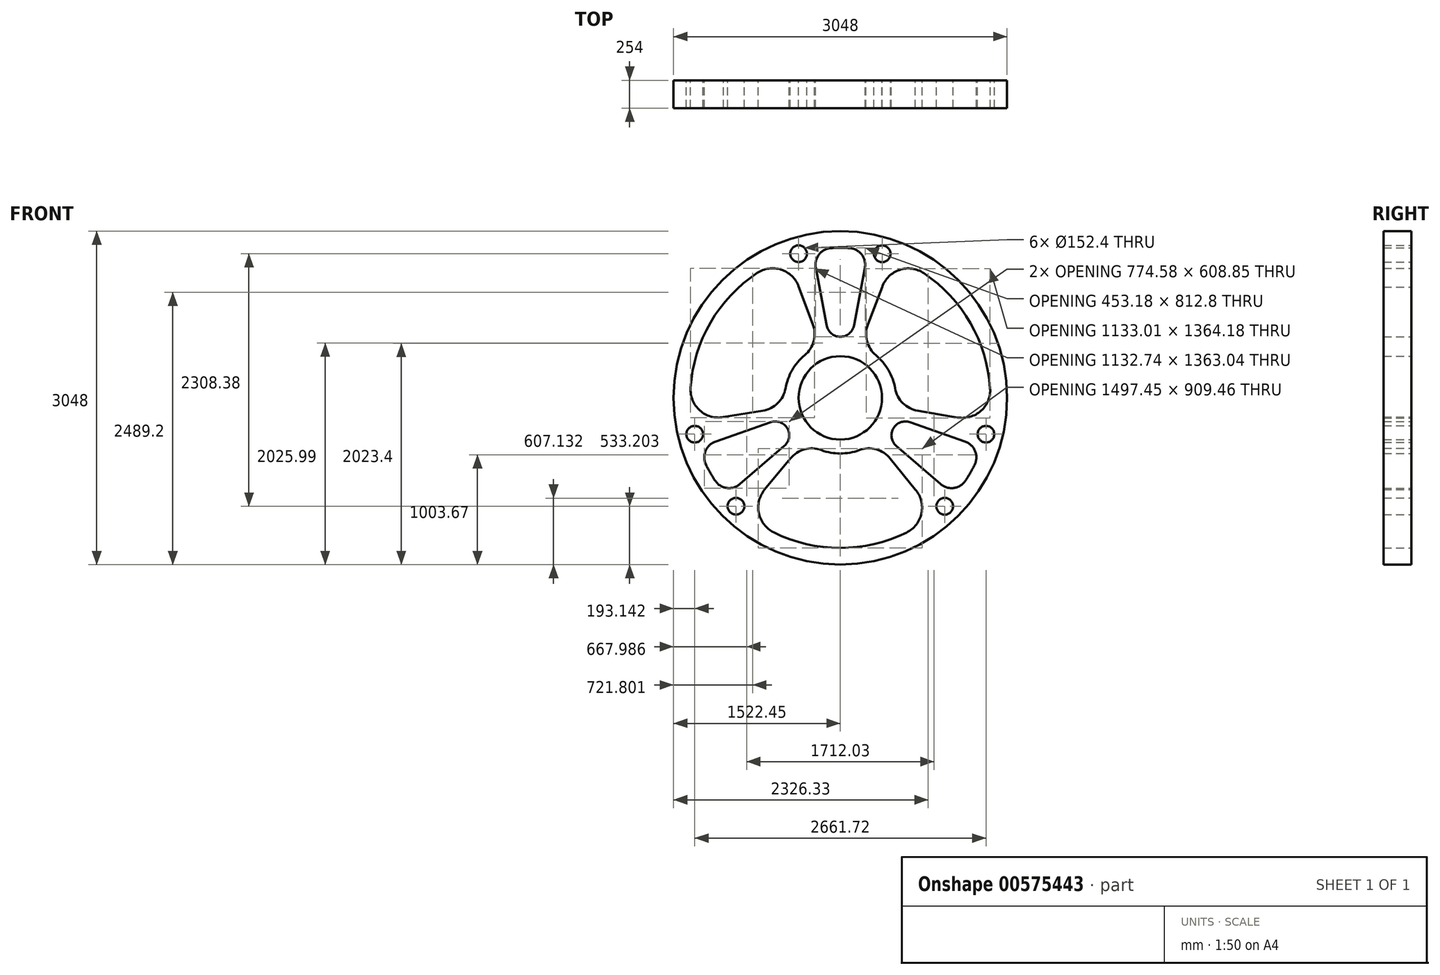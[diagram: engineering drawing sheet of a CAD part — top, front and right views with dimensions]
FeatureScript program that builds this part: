
annotation { "Feature Type Name" : "Feature", "Feature Type Description" : "" }
export const myFeature = defineFeature(function(context is Context, id is Id, definition is map)
    precondition{}
    {
        {
            var Q0;
            Q0=qCreatedBy(makeId("Front.planeOp"),FACE);
            var sketch = newSketch(context, id + "F0", { "sketchPlane" : qUnion([Q0])});
            skCircle(sketch, "E0", {"center": v(0, 0) * mm, "radius": 1524 * mm});
            skArc(sketch, "E1", {"start": v(-173.99, -477.28) * mm, "mid": v(0, -508) * mm, "end": v(173.99, -477.28) * mm});
            skLineSegment(sketch, "E2", {"start": v(0, 0) * mm, "end": v(0, 0) * mm});
            skArc(sketch, "E3", {"start": v(-173.99, -477.28) * mm, "mid": v(-327.72, -470.84) * mm, "end": v(-456.96, -554.34) * mm});
            skArc(sketch, "E4", {"start": v(-692.3, -839.79) * mm, "mid": v(-744.7, -1054.46) * mm, "end": v(-609.1, -1228.94) * mm});
            skArc(sketch, "E5", {"start": v(456.97, -554.35) * mm, "mid": v(327.73, -470.84) * mm, "end": v(173.99, -477.28) * mm});
            skArc(sketch, "E6", {"start": v(605.37, -1230.78) * mm, "mid": v(742.1, -1053.78) * mm, "end": v(685.9, -837.3) * mm});
            skArc(sketch, "E7.trimOffspring", {"start": v(500.33, 87.96) * mm, "mid": v(439.94, 254) * mm, "end": v(326.34, 389.31) * mm});
            skLineSegment(sketch, "E8.trimOffspring", {"start": v(-456.96, -554.34) * mm, "end": v(-692.3, -839.79) * mm});
            skLineSegment(sketch, "E9.trimOffspring", {"start": v(456.97, -554.35) * mm, "end": v(685.9, -837.3) * mm});
            skArc(sketch, "E10", {"start": v(-83.52, 1369.05) * mm, "mid": v(-194.47, 1310.6) * mm, "end": v(-224, 1188.72) * mm});
            skArc(sketch, "E11", {"start": v(224, 1188.72) * mm, "mid": v(194.47, 1310.6) * mm, "end": v(83.52, 1369.05) * mm});
            skArc(sketch, "E12", {"start": v(-124.8, 662.28) * mm, "mid": v(0, 558.8) * mm, "end": v(124.8, 662.28) * mm});
            skLineSegment(sketch, "E13", {"start": v(-224, 1188.72) * mm, "end": v(-124.8, 662.28) * mm});
            skLineSegment(sketch, "E14", {"start": v(224, 1188.72) * mm, "end": v(124.8, 662.28) * mm});
            skArc(sketch, "E15.trimOffspring", {"start": v(83.52, 1369.05) * mm, "mid": v(0, 1371.6) * mm, "end": v(-83.52, 1369.05) * mm});
            skLineSegment(sketch, "E16.trimOffspring", {"start": v(124.8, 662.28) * mm, "end": v(224, 1188.72) * mm});
            skLineSegment(sketch, "E17.trimOffspring", {"start": v(-124.8, 662.28) * mm, "end": v(-224, 1188.72) * mm});
            skArc(sketch, "E18.1.0", {"start": v(251.6, 672.92) * mm, "mid": v(243.9, 519.24) * mm, "end": v(326.34, 389.31) * mm});
            skArc(sketch, "E18.1.2", {"start": v(500.33, 87.96) * mm, "mid": v(571.62, -48.4) * mm, "end": v(708.55, -118.57) * mm});
            skLineSegment(sketch, "E18.1.3", {"start": v(708.55, -118.57) * mm, "end": v(1073.42, -179.65) * mm});
            skArc(sketch, "E18.1.4", {"start": v(1073.42, -179.65) * mm, "mid": v(1285.53, -117.7) * mm, "end": v(1368.84, 86.97) * mm});
            skArc(sketch, "E18.1.5", {"start": v(763.2, 1139.65) * mm, "mid": v(541.55, 1169.57) * mm, "end": v(382.17, 1012.65) * mm});
            skLineSegment(sketch, "E18.1.6", {"start": v(251.6, 672.92) * mm, "end": v(382.17, 1012.65) * mm});
            skArc(sketch, "E18.2.0", {"start": v(-708.57, -118.57) * mm, "mid": v(-571.62, -48.4) * mm, "end": v(-500.33, 87.96) * mm});
            skArc(sketch, "E18.2.2", {"start": v(-326.34, 389.31) * mm, "mid": v(-243.9, 519.23) * mm, "end": v(-251.6, 672.91) * mm});
            skLineSegment(sketch, "E18.2.3", {"start": v(-251.6, 672.91) * mm, "end": v(-381.13, 1019.44) * mm});
            skArc(sketch, "E18.2.4", {"start": v(-381.13, 1019.44) * mm, "mid": v(-540.84, 1172.15) * mm, "end": v(-759.74, 1141.96) * mm});
            skArc(sketch, "E18.2.5", {"start": v(-1368.57, 91.12) * mm, "mid": v(-1283.65, -115.8) * mm, "end": v(-1068.07, -175.35) * mm});
            skLineSegment(sketch, "E18.2.6", {"start": v(-708.57, -118.57) * mm, "end": v(-1068.07, -175.35) * mm});
            skLineSegment(sketch, "E19.1.0", {"start": v(-635.95, -223.06) * mm, "end": v(-1141.46, -400.36) * mm});
            skLineSegment(sketch, "E19.1.1", {"start": v(-917.45, -788.35) * mm, "end": v(-511.15, -439.22) * mm});
            skArc(sketch, "E19.1.2", {"start": v(-1143.87, -756.86) * mm, "mid": v(-1037.77, -823.71) * mm, "end": v(-917.45, -788.35) * mm});
            skArc(sketch, "E19.1.3", {"start": v(-1227.4, -612.2) * mm, "mid": v(-1187.84, -685.8) * mm, "end": v(-1143.87, -756.86) * mm});
            skArc(sketch, "E19.1.4", {"start": v(-1141.46, -400.36) * mm, "mid": v(-1232.24, -486.88) * mm, "end": v(-1227.4, -612.2) * mm});
            skArc(sketch, "E19.1.5", {"start": v(-511.15, -439.22) * mm, "mid": v(-483.93, -279.4) * mm, "end": v(-635.95, -223.06) * mm});
            skLineSegment(sketch, "E19.2.0", {"start": v(511.15, -439.22) * mm, "end": v(917.45, -788.35) * mm});
            skLineSegment(sketch, "E19.2.1", {"start": v(1141.46, -400.36) * mm, "end": v(635.95, -223.06) * mm});
            skArc(sketch, "E19.2.2", {"start": v(1227.4, -612.2) * mm, "mid": v(1232.24, -486.88) * mm, "end": v(1141.46, -400.36) * mm});
            skArc(sketch, "E19.2.3", {"start": v(1143.87, -756.86) * mm, "mid": v(1187.84, -685.8) * mm, "end": v(1227.4, -612.2) * mm});
            skArc(sketch, "E19.2.4", {"start": v(917.45, -788.35) * mm, "mid": v(1037.77, -823.71) * mm, "end": v(1143.87, -756.86) * mm});
            skArc(sketch, "E19.2.5", {"start": v(635.95, -223.06) * mm, "mid": v(483.93, -279.4) * mm, "end": v(511.15, -439.22) * mm});
            skCircle(sketch, "E20", {"center": v(-381.13, 1317.58) * mm, "radius": 76.2 * mm});
            skCircle(sketch, "E21.1.0", {"center": v(-953.56, -989.74) * mm, "radius": 76.2 * mm});
            skCircle(sketch, "E21.2.0", {"center": v(1330.86, -331.82) * mm, "radius": 76.2 * mm});
            skPoint(sketch, "E21.center", {"position": v(-1.28, -1.33) * mm});
            skCircle(sketch, "E22", {"center": v(382.17, 1317.28) * mm, "radius": 76.2 * mm});
            skCircle(sketch, "E23.1.0", {"center": v(-1330.86, -331.82) * mm, "radius": 76.2 * mm});
            skCircle(sketch, "E23.2.0", {"center": v(953.82, -990.8) * mm, "radius": 76.2 * mm});
            skPoint(sketch, "E23.center", {"position": v(1.71, -1.78) * mm});
            skArc(sketch, "E24.trimOffspring", {"start": v(-326.34, 389.31) * mm, "mid": v(-439.94, 254) * mm, "end": v(-500.33, 87.96) * mm});
            skPoint(sketch, "E25.orphan", {"position": v(326.34, 389.31) * mm});
            skPoint(sketch, "E26.orphan", {"position": v(-326.34, 389.31) * mm});
            skCircle(sketch, "E27", {"center": v(0, 0) * mm, "radius": 381 * mm});
            skArc(sketch, "E28", {"start": v(-98.43, -25.2) * mm, "mid": v(-71.84, -71.84) * mm, "end": v(-25.2, -98.42) * mm});
            skArc(sketch, "E29", {"start": v(-25.2, -98.43) * mm, "mid": v(0, -127) * mm, "end": v(25.2, -98.43) * mm});
            skArc(sketch, "E30", {"start": v(98.43, -25.2) * mm, "mid": v(127, 0) * mm, "end": v(98.43, 25.2) * mm});
            skArc(sketch, "E31", {"start": v(-98.43, 25.2) * mm, "mid": v(-127, 0) * mm, "end": v(-98.43, -25.2) * mm});
            skArc(sketch, "E32", {"start": v(25.2, 98.43) * mm, "mid": v(0, 127) * mm, "end": v(-25.2, 98.43) * mm});
            skArc(sketch, "E33.trimOffspring", {"start": v(98.43, 25.2) * mm, "mid": v(71.84, 71.84) * mm, "end": v(25.2, 98.43) * mm});
            skArc(sketch, "E34.trimOffspring", {"start": v(25.2, -98.43) * mm, "mid": v(71.84, -71.84) * mm, "end": v(98.42, -25.2) * mm});
            skArc(sketch, "E35.trimOffspring", {"start": v(-25.2, 98.43) * mm, "mid": v(-71.84, 71.84) * mm, "end": v(-98.42, 25.2) * mm});
            skCircle(sketch, "E36", {"center": v(101.6, 113.6) * mm, "radius": 50.8 * mm});
            skCircle(sketch, "E37", {"center": v(101.6, -113.6) * mm, "radius": 50.8 * mm});
            skCircle(sketch, "E38", {"center": v(-101.6, -113.6) * mm, "radius": 50.8 * mm});
            skCircle(sketch, "E39", {"center": v(-101.6, 113.6) * mm, "radius": 50.8 * mm});
            skCircle(sketch, "E40", {"center": v(255.7, 0) * mm, "radius": 50.8 * mm});
            skPoint(sketch, "E40.centerSnap0", {"position": v(127, 0) * mm});
            skCircle(sketch, "E41", {"center": v(-252.28, 0) * mm, "radius": 50.8 * mm});
            skPoint(sketch, "E41.centerSnap0", {"position": v(-127, 0) * mm});
            skCircle(sketch, "E42", {"center": v(0, 252.22) * mm, "radius": 50.8 * mm});
            skPoint(sketch, "E42.centerSnap0", {"position": v(0, 127) * mm});
            skCircle(sketch, "E43", {"center": v(0, -255.77) * mm, "radius": 50.8 * mm});
            skPoint(sketch, "E43.centerSnap0", {"position": v(0, -127) * mm});
            skArc(sketch, "E44.trimOffspring", {"start": v(-609.1, -1228.94) * mm, "mid": v(-2.08, -1371.6) * mm, "end": v(605.37, -1230.78) * mm});
            skArc(sketch, "E45.trimOffspring", {"start": v(1368.84, 86.97) * mm, "mid": v(1188.88, 684) * mm, "end": v(763.2, 1139.65) * mm});
            skArc(sketch, "E46.trimOffspring", {"start": v(-759.74, 1141.96) * mm, "mid": v(-1186.8, 687.6) * mm, "end": v(-1368.57, 91.12) * mm});
            skCircle(sketch, "E47", {"center": v(1.71, -1.78) * mm, "radius": 254 * mm});
            skSolve(sketch);
        }
        {
            var Q0;
            Q0 = qSketchRegion(id + "F0", true);
            extrude(context, id + "F1", {"entities" : qUnion([Q0]), "depth" : 254 * mm, "offsetDistance" : 25.4 * mm, "symmetric" : true});
        }
    });
